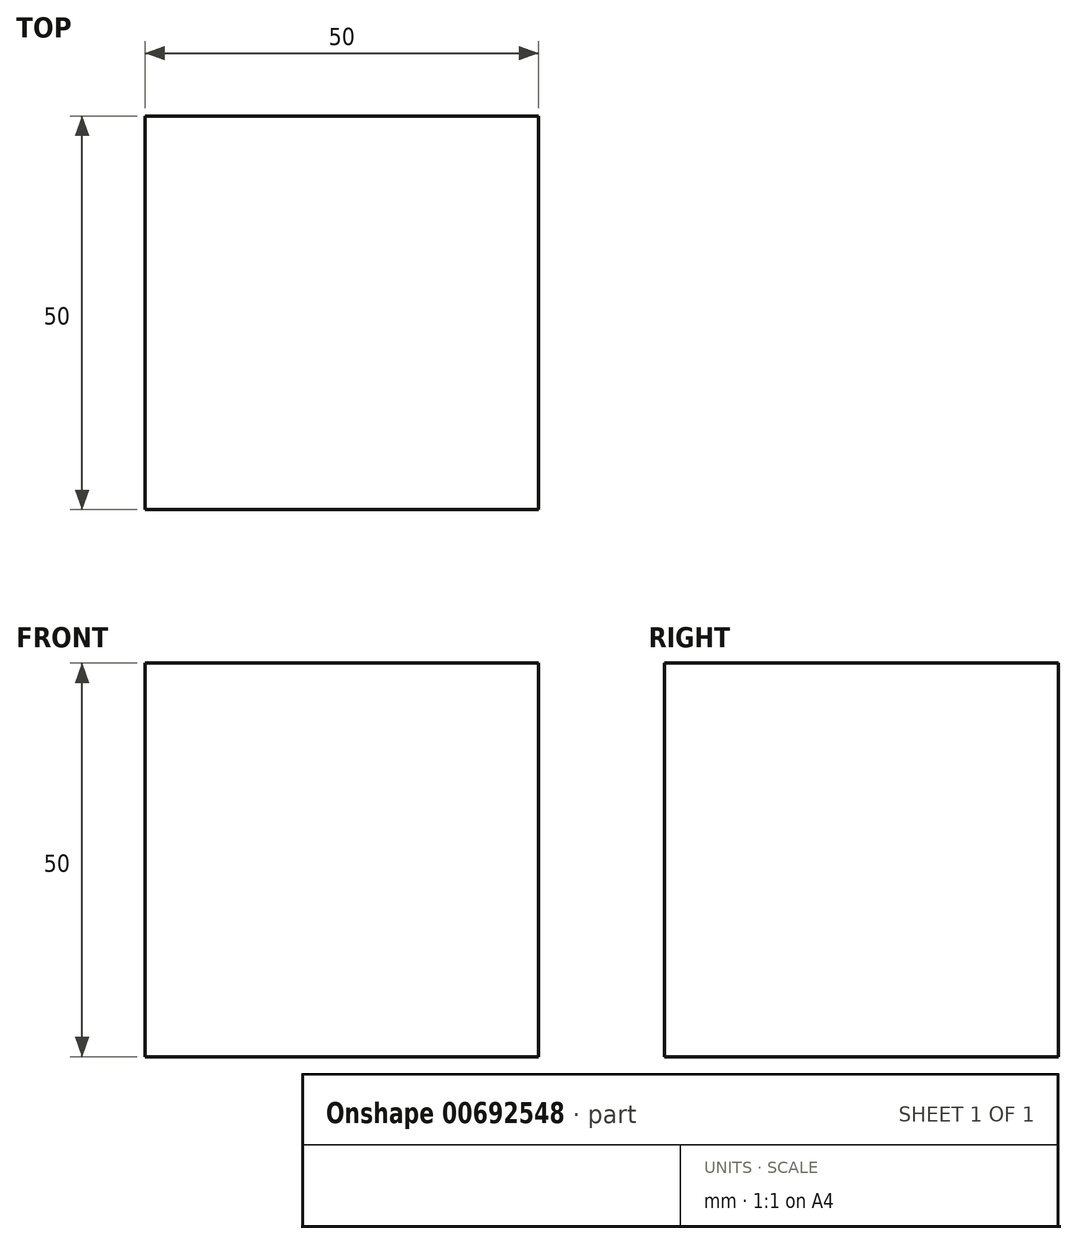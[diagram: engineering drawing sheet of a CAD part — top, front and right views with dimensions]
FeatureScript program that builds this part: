
annotation { "Feature Type Name" : "Feature", "Feature Type Description" : "" }
export const myFeature = defineFeature(function(context is Context, id is Id, definition is map)
    precondition{}
    {
        {
            var Q0;
            Q0=qCreatedBy(makeId("Top.planeOp"),FACE);
            var sketch = newSketch(context, id + "F0", { "sketchPlane" : qUnion([Q0])});
            skLineSegment(sketch, "E0.bottom", {"start": v(-23.26, 16.79) * mm, "end": v(26.74, 16.79) * mm});
            skLineSegment(sketch, "E0.top", {"start": v(-23.26, -33.21) * mm, "end": v(26.74, -33.21) * mm});
            skLineSegment(sketch, "E0.left", {"start": v(-23.26, 16.79) * mm, "end": v(-23.26, -33.21) * mm});
            skLineSegment(sketch, "E0.right", {"start": v(26.74, 16.79) * mm, "end": v(26.74, -33.21) * mm});
            skSolve(sketch);
        }
        {
            var Q0;
            Q0=makeQuery(id+"F0.imprint","IMPRINT",FACE,{"disambiguationData":[TD([[makeQuery(id+"F0.imprint","IMPRINT",EDGE,{"derivedFrom":sQuery(id+"F0.wireOp",EDGE,"E0.bottom")}),-1.0]])]});
            extrude(context, id + "F1", {"entities" : qUnion([Q0]), "depth" : 50 * mm, "offsetDistance" : 25.4 * mm});
        }
    });
